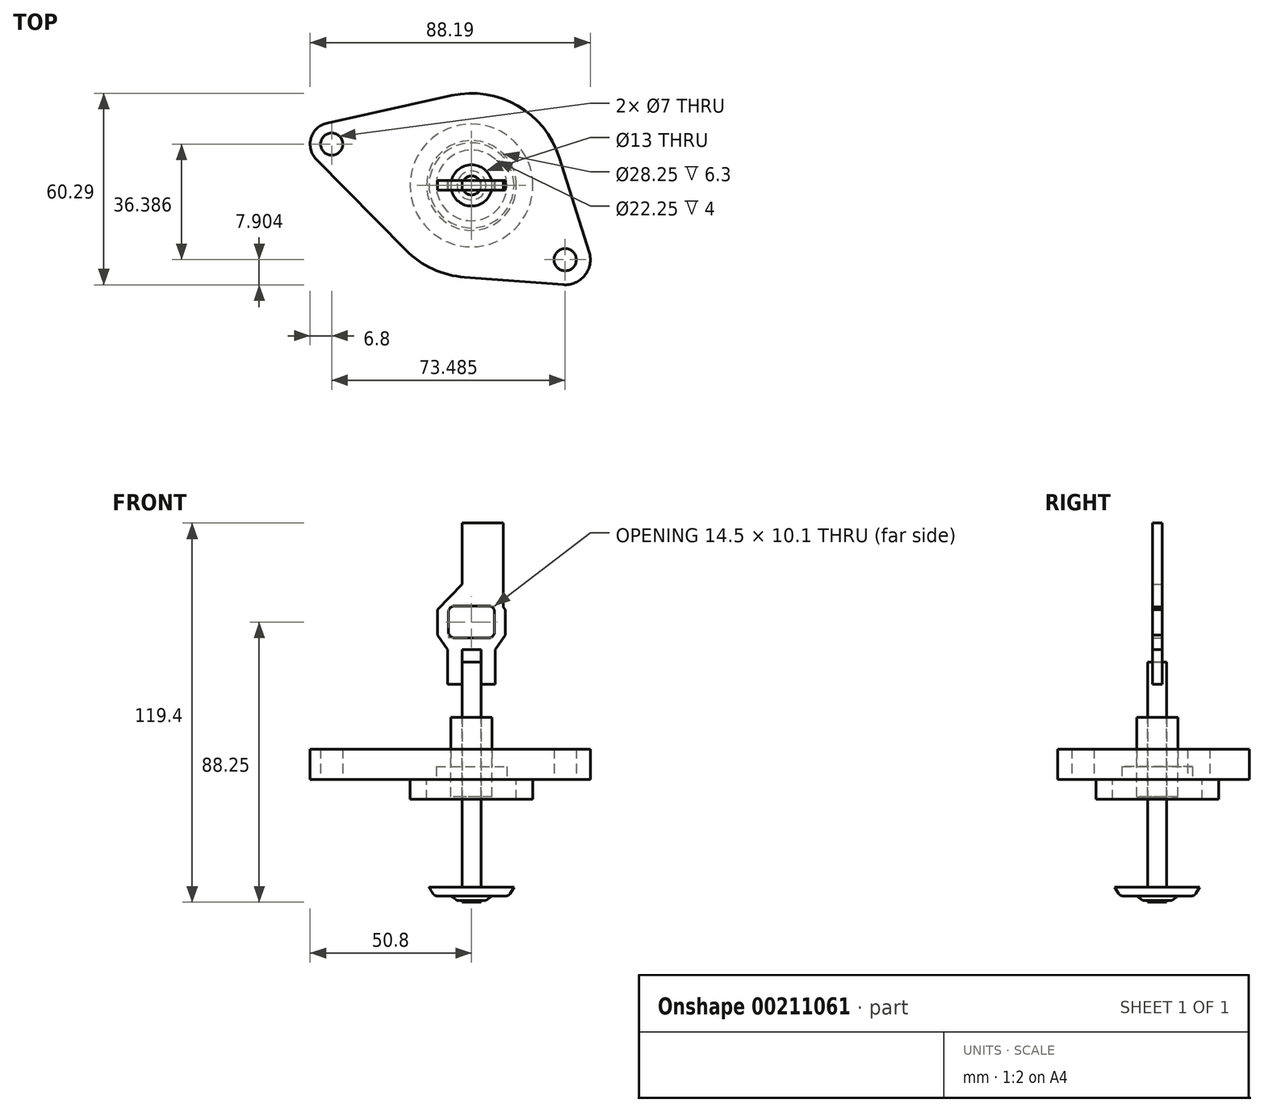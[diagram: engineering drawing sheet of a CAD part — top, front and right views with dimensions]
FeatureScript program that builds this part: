
annotation { "Feature Type Name" : "Feature", "Feature Type Description" : "" }
export const myFeature = defineFeature(function(context is Context, id is Id, definition is map)
    precondition{}
    {
        {
            var Q0;
            Q0=qCreatedBy(makeId("Top.planeOp"),FACE);
            var sketch = newSketch(context, id + "F0", { "sketchPlane" : qUnion([Q0])});
            skCircle(sketch, "E0", {"center": v(0, 0) * mm, "radius": 6.5 * mm});
            skCircle(sketch, "E1", {"center": v(-44, 13) * mm, "radius": 3.5 * mm});
            skCircle(sketch, "E2", {"center": v(29.49, -23.39) * mm, "radius": 3.5 * mm});
            skArc(sketch, "E3", {"start": v(-45.47, 19.64) * mm, "mid": v(-50.52, 14.93) * mm, "end": v(-48.84, 8.23) * mm});
            skArc(sketch, "E4", {"start": v(28.9, -31.26) * mm, "mid": v(35.67, -28.3) * mm, "end": v(37.02, -21.01) * mm});
            skArc(sketch, "E5", {"start": v(27.66, 8.71) * mm, "mid": v(14.5, 25.1) * mm, "end": v(-6.27, 28.31) * mm});
            skArc(sketch, "E6", {"start": v(-20.65, -20.36) * mm, "mid": v(-12.2, -26.31) * mm, "end": v(-2.18, -28.92) * mm});
            skLineSegment(sketch, "E7", {"start": v(-45.47, 19.64) * mm, "end": v(-6.27, 28.31) * mm});
            skLineSegment(sketch, "E8", {"start": v(-48.84, 8.23) * mm, "end": v(-20.65, -20.36) * mm});
            skLineSegment(sketch, "E9", {"start": v(27.66, 8.71) * mm, "end": v(37.02, -21.01) * mm});
            skLineSegment(sketch, "E10", {"start": v(-2.18, -28.92) * mm, "end": v(28.9, -31.26) * mm});
            skSolve(sketch);
        }
        {
            var Q0;
            Q0 = qSketchRegion(id + "F0", true);
            extrude(context, id + "F1", {"entities" : qUnion([Q0]), "depth" : 9.5 * mm});
        }
        {
            var Q0;
            Q0=makeQuery(id+"F1.opExtrude","CAP_FACE",FACE,{"disambiguationData":[OSD([sQuery(id+"F0.wireOp",EDGE,"E0"),sQuery(id+"F0.wireOp",EDGE,"E1"),sQuery(id+"F0.wireOp",EDGE,"E2"),sQuery(id+"F0.wireOp",EDGE,"E3"),sQuery(id+"F0.wireOp",EDGE,"E4"),sQuery(id+"F0.wireOp",EDGE,"E5"),sQuery(id+"F0.wireOp",EDGE,"E6"),sQuery(id+"F0.wireOp",EDGE,"E7"),sQuery(id+"F0.wireOp",EDGE,"E8"),sQuery(id+"F0.wireOp",EDGE,"E9"),sQuery(id+"F0.wireOp",EDGE,"E10")])],"isStart":true});
            var sketch = newSketch(context, id + "F2", { "sketchPlane" : qUnion([Q0])});
            skCircle(sketch, "E11", {"center": v(0, 0) * mm, "radius": 19.32 * mm});
            skCircle(sketch, "E12", {"center": v(0, 0) * mm, "radius": 14.12 * mm});
            skSolve(sketch);
        }
        {
            var Q0;
            Q0 = qSketchRegion(id + "F2", true);
            extrude(context, id + "F3", {"entities" : qUnion([Q0]), "operationType" : NewBodyOperationType.ADD, "depth" : 6.3 * mm});
        }
        {
            var Q0;
            {var subQ0=sQuery(id+"F0.wireOp",EDGE,"E0");Q0=makeQuery(id+"F3.boolean.opBoolean","SPLIT",FACE,{"disambiguationData":[TD([makeQuery(id+"F1.opExtrude","SWEPT_FACE",FACE,{"disambiguationData":[OSD([subQ0])]})])],"derivedFrom":makeQuery(id+"F1.opExtrude","CAP_FACE",FACE,{"disambiguationData":[OSD([subQ0,sQuery(id+"F0.wireOp",EDGE,"E1"),sQuery(id+"F0.wireOp",EDGE,"E2"),sQuery(id+"F0.wireOp",EDGE,"E3"),sQuery(id+"F0.wireOp",EDGE,"E4"),sQuery(id+"F0.wireOp",EDGE,"E5"),sQuery(id+"F0.wireOp",EDGE,"E6"),sQuery(id+"F0.wireOp",EDGE,"E7"),sQuery(id+"F0.wireOp",EDGE,"E8"),sQuery(id+"F0.wireOp",EDGE,"E9"),sQuery(id+"F0.wireOp",EDGE,"E10")])],"isStart":true})});}
            var sketch = newSketch(context, id + "F4", { "sketchPlane" : qUnion([Q0])});
            skCircle(sketch, "E13", {"center": v(0, 0) * mm, "radius": 11.12 * mm});
            skSolve(sketch);
        }
        {
            var Q0;
            Q0 = qSketchRegion(id + "F4", true);
            extrude(context, id + "F5", {"entities" : qUnion([Q0]), "operationType" : NewBodyOperationType.REMOVE, "oppositeDirection" : true, "depth" : 4 * mm});
        }
        {
            var Q0;
            Q0=makeQuery(id+"F1.opExtrude","CAP_FACE",FACE,{"disambiguationData":[OSD([sQuery(id+"F0.wireOp",EDGE,"E0"),sQuery(id+"F0.wireOp",EDGE,"E1"),sQuery(id+"F0.wireOp",EDGE,"E2"),sQuery(id+"F0.wireOp",EDGE,"E3"),sQuery(id+"F0.wireOp",EDGE,"E4"),sQuery(id+"F0.wireOp",EDGE,"E5"),sQuery(id+"F0.wireOp",EDGE,"E6"),sQuery(id+"F0.wireOp",EDGE,"E7"),sQuery(id+"F0.wireOp",EDGE,"E8"),sQuery(id+"F0.wireOp",EDGE,"E9"),sQuery(id+"F0.wireOp",EDGE,"E10")])],"isStart":false});
            var sketch = newSketch(context, id + "F6", { "sketchPlane" : qUnion([Q0])});
            skCircle(sketch, "E14", {"center": v(0, 0) * mm, "radius": 6.5 * mm});
            skCircle(sketch, "E15", {"center": v(0, 0) * mm, "radius": 3 * mm});
            skSolve(sketch);
        }
        {
            var Q0;
            Q0 = qSketchRegion(id + "F6", true);
            extrude(context, id + "F7", {"entities" : qUnion([Q0]), "oppositeDirection" : true, "depth" : 15 * mm, "hasSecondDirection" : true, "secondDirectionOppositeDirection" : false, "secondDirectionDepth" : 10 * mm});
        }
        {
            var Q0;
            Q0=qCreatedBy(makeId("Front.planeOp"),FACE);
            var sketch = newSketch(context, id + "F8", { "sketchPlane" : qUnion([Q0])});
            skLineSegment(sketch, "E16", {"start": v(0, 36.9) * mm, "end": v(-2.98, 36.9) * mm});
            skLineSegment(sketch, "E17", {"start": v(-2.98, 36.9) * mm, "end": v(-2.97, -34) * mm});
            skLineSegment(sketch, "E18", {"start": v(-2.98, -34) * mm, "end": v(-13.37, -34) * mm});
            skLineSegment(sketch, "E19", {"start": v(-13.37, -34) * mm, "end": v(-11.7, -36.7) * mm});
            skLineSegment(sketch, "E20", {"start": v(-11.7, -36.7) * mm, "end": v(-6.5, -36.7) * mm});
            skLineSegment(sketch, "E21", {"start": v(-6.5, -36.7) * mm, "end": v(-4.55, -38.1) * mm});
            skLineSegment(sketch, "E22", {"start": v(-4.55, -38.1) * mm, "end": v(-2.98, -38.1) * mm});
            skLineSegment(sketch, "E23", {"start": v(-2.97, -38.1) * mm, "end": v(-2.97, -38.7) * mm});
            skLineSegment(sketch, "E24", {"start": v(-2.97, -38.7) * mm, "end": v(0, -38.7) * mm});
            skLineSegment(sketch, "E25", {"start": v(0, -38.7) * mm, "end": v(0, 36.9) * mm});
            skSolve(sketch);
        }
        {
            var Q0;
            Q0 = qSketchRegion(id + "F8", true);
            var Q1;
            Q1=sQuery(id+"F8.wireOp",EDGE,"E25");
            revolve(context, id + "F9", {"entities" : qUnion([Q0]), "axis" : qUnion([Q1]), "revolveType" : RevolveType.FULL});
        }
        {
            var Q0;
            Q0=makeQuery(id+"F9.opRevolve","SWEPT_EDGE",EDGE,{"disambiguationData":[OSD([sQuery(id+"F8.wireOp",EDGE,"E19"),sQuery(id+"F8.wireOp",EDGE,"E20")])]});
            fillet(context, id + "F10", {"entities" : qUnion([Q0]), "radius" : 1.5 * mm, "tangentPropagation" : true, "allowEdgeOverflow" : false});
        }
        {
            var Q0;
            Q0=qCreatedBy(makeId("Front.planeOp"),FACE);
            var sketch = newSketch(context, id + "F11", { "sketchPlane" : qUnion([Q0])});
            skLineSegment(sketch, "E26", {"start": v(2.97, 29.9) * mm, "end": v(7.47, 29.9) * mm});
            skLineSegment(sketch, "E27", {"start": v(7.47, 29.9) * mm, "end": v(7.47, 40.9) * mm});
            skLineSegment(sketch, "E28", {"start": v(7.47, 40.9) * mm, "end": v(10.65, 45.37) * mm});
            skLineSegment(sketch, "E29", {"start": v(10.65, 45.37) * mm, "end": v(10.65, 53.37) * mm});
            skLineSegment(sketch, "E30", {"start": v(10.65, 53.37) * mm, "end": v(10.03, 54.24) * mm});
            skLineSegment(sketch, "E31", {"start": v(10.03, 54.24) * mm, "end": v(10.03, 80.7) * mm});
            skLineSegment(sketch, "E32", {"start": v(10.03, 80.7) * mm, "end": v(-2.97, 80.7) * mm});
            skLineSegment(sketch, "E33", {"start": v(-2.98, 80.7) * mm, "end": v(-2.97, 61.41) * mm});
            skLineSegment(sketch, "E34", {"start": v(-2.98, 61.41) * mm, "end": v(-10.65, 53.37) * mm});
            skLineSegment(sketch, "E35", {"start": v(-10.65, 53.37) * mm, "end": v(-10.65, 45.37) * mm});
            skLineSegment(sketch, "E36", {"start": v(-10.65, 45.37) * mm, "end": v(-7.47, 40.9) * mm});
            skLineSegment(sketch, "E37", {"start": v(-7.47, 40.9) * mm, "end": v(-7.47, 29.9) * mm});
            skLineSegment(sketch, "E38", {"start": v(-7.47, 29.9) * mm, "end": v(-2.97, 29.9) * mm});
            skLineSegment(sketch, "E39", {"start": v(-2.97, 29.9) * mm, "end": v(-2.98, 40.9) * mm});
            skLineSegment(sketch, "E40", {"start": v(-2.98, 40.9) * mm, "end": v(2.98, 40.9) * mm});
            skLineSegment(sketch, "E41", {"start": v(2.97, 40.9) * mm, "end": v(2.97, 29.9) * mm});
            skLineSegment(sketch, "E42.bottom", {"start": v(-7.25, 44.5) * mm, "end": v(7.25, 44.5) * mm});
            skLineSegment(sketch, "E42.top", {"start": v(-7.25, 54.6) * mm, "end": v(7.25, 54.6) * mm});
            skLineSegment(sketch, "E42.left", {"start": v(-7.25, 44.5) * mm, "end": v(-7.25, 54.6) * mm});
            skLineSegment(sketch, "E42.right", {"start": v(7.25, 44.5) * mm, "end": v(7.25, 54.6) * mm});
            skLineSegment(sketch, "E43", {"start": v(7.25, 49.67) * mm, "end": v(10.65, 49.67) * mm, "construction": true});
            skLineSegment(sketch, "E44", {"start": v(-7.25, 50) * mm, "end": v(-10.65, 50) * mm, "construction": true});
            skSolve(sketch);
        }
        {
            var Q0;
            Q0 = qSketchRegion(id + "F11", true);
            extrude(context, id + "F12", {"entities" : qUnion([Q0]), "endBound" : BoundingType.SYMMETRIC, "depth" : 3 * mm});
        }
        {
            var Q0;
            Q0=makeQuery(id+"F12.opExtrude","SWEPT_EDGE",EDGE,{"disambiguationData":[OSD([sQuery(id+"F11.wireOp",EDGE,"E42.top"),sQuery(id+"F11.wireOp",EDGE,"E42.right")])]});
            var Q1;
            Q1=makeQuery(id+"F12.opExtrude","SWEPT_EDGE",EDGE,{"disambiguationData":[OSD([sQuery(id+"F11.wireOp",EDGE,"E42.bottom"),sQuery(id+"F11.wireOp",EDGE,"E42.right")])]});
            var Q2;
            Q2=makeQuery(id+"F12.opExtrude","SWEPT_EDGE",EDGE,{"disambiguationData":[OSD([sQuery(id+"F11.wireOp",EDGE,"E42.bottom"),sQuery(id+"F11.wireOp",EDGE,"E42.left")])]});
            var Q3;
            Q3=makeQuery(id+"F12.opExtrude","SWEPT_EDGE",EDGE,{"disambiguationData":[OSD([sQuery(id+"F11.wireOp",EDGE,"E42.top"),sQuery(id+"F11.wireOp",EDGE,"E42.left")])]});
            fillet(context, id + "F13", {"entities" : qUnion([Q0, Q1, Q2, Q3]), "radius" : 2 * mm, "tangentPropagation" : true, "allowEdgeOverflow" : false});
        }
    });
